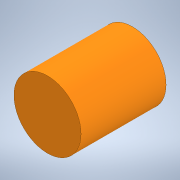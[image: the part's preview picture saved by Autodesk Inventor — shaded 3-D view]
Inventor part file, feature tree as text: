
AUTODESK INVENTOR PART (.ipt)
format: ipt  version: 2020 (Build 240168000, 168)  size: 93,696 bytes
history: native  units: mm
features: extrude x1, sketch x1
ambient origin geometry x8: Origin, YZ Plane, XZ Plane, XY Plane, X Axis, Y Axis, Z Axis, Center Point
bodies: Solid1 (feature_tree)
feature tree (2):
  extrude  "Extrusion1"  Depth=95.0mm TaperAngle=0.0deg
  sketch  "Sketch1"  dims[d0=75.0mm d1=95.0mm d2=0.0mm]
